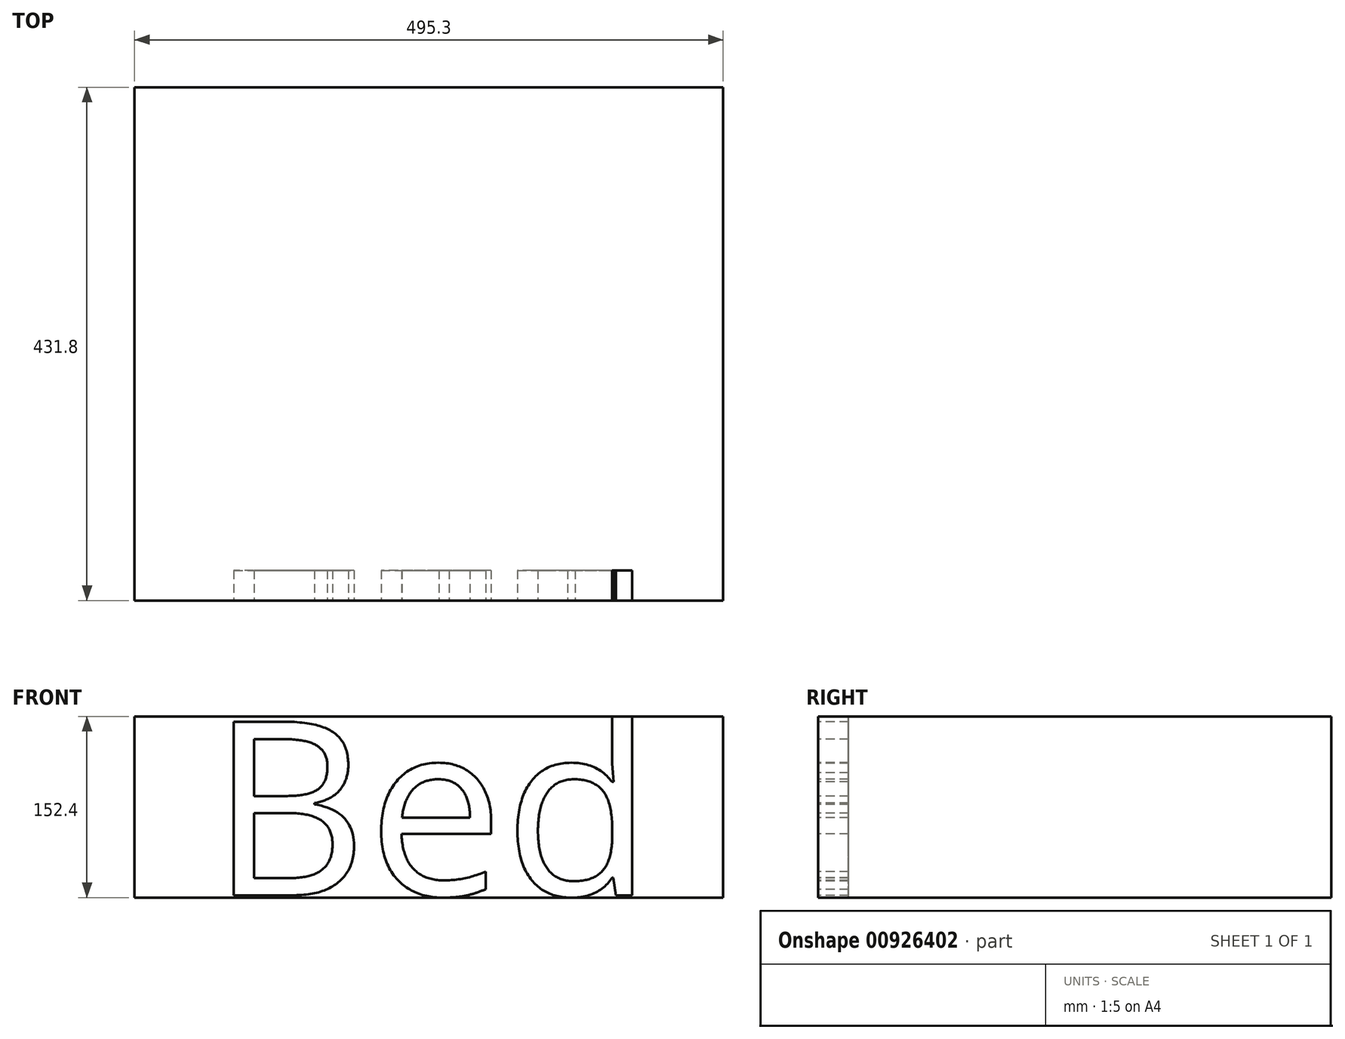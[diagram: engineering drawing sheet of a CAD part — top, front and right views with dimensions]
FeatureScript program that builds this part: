
annotation { "Feature Type Name" : "Feature", "Feature Type Description" : "" }
export const myFeature = defineFeature(function(context is Context, id is Id, definition is map)
    precondition{}
    {
        {
            var Q0;
            Q0=qCreatedBy(makeId("Front.planeOp"),FACE);
            var sketch = newSketch(context, id + "F0", { "sketchPlane" : qUnion([Q0])});
            skLineSegment(sketch, "E0.bottom", {"start": v(247.65, -76.2) * mm, "end": v(-247.65, -76.2) * mm});
            skLineSegment(sketch, "E0.top", {"start": v(247.65, 76.2) * mm, "end": v(-247.65, 76.2) * mm});
            skLineSegment(sketch, "E0.left", {"start": v(247.65, -76.2) * mm, "end": v(247.65, 76.2) * mm});
            skLineSegment(sketch, "E0.right", {"start": v(-247.65, -76.2) * mm, "end": v(-247.65, 76.2) * mm});
            skPoint(sketch, "E0.middle", {"position": v(0, 0) * mm});
            skSolve(sketch);
        }
        {
            var Q0;
            Q0=makeQuery(id+"F0.imprint","IMPRINT",FACE,{"disambiguationData":[TD([[makeQuery(id+"F0.imprint","IMPRINT",EDGE,{"derivedFrom":sQuery(id+"F0.wireOp",EDGE,"E0.bottom")}),-1.0]])]});
            extrude(context, id + "F1", {"entities" : qUnion([Q0]), "depth" : 431.8 * mm, "offsetDistance" : 25.4 * mm});
        }
        {
            var Q0;
            Q0=makeQuery(id+"F1.opExtrude","CAP_FACE",FACE,{"disambiguationData":[OSD([sQuery(id+"F0.wireOp",EDGE,"E0.bottom"),sQuery(id+"F0.wireOp",EDGE,"E0.top"),sQuery(id+"F0.wireOp",EDGE,"E0.left"),sQuery(id+"F0.wireOp",EDGE,"E0.right")])],"isStart":false});
            var sketch = newSketch(context, id + "F2", { "sketchPlane" : qUnion([Q0])});
            skText(sketch, "E1", { "text": "Bed\n", "fontName": "OpenSans-Regular.ttf"});
            const initialGuessF2  = {"E1": [-0.18415, -0.07427, 1, 0, 0.14726]};
            skSetInitialGuess(sketch, initialGuessF2);
            skSolve(sketch);
        }
        {
            var Q0;
            Q0 = qSketchRegion(id + "F2", true);
            extrude(context, id + "F3", {"entities" : qUnion([Q0]), "operationType" : NewBodyOperationType.REMOVE, "oppositeDirection" : true, "depth" : 25.4 * mm, "offsetDistance" : 25.4 * mm});
        }
    });
